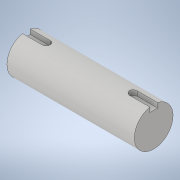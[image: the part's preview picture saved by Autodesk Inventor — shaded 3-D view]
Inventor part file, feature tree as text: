
AUTODESK INVENTOR PART (.ipt)
format: ipt  version: 2021 (Build 250183000, 183)  size: 124,928 bytes
history: native  units: in
note: dims shown in document units (in); Inventor stores cm internally (conversion verified against a paired STEP export)
features: extrude x3, sketch x3, plane x1, mirror x1
ambient origin geometry x8: Origin, YZ Plane, XZ Plane, XY Plane, X Axis, Y Axis, Z Axis, Center Point
bodies: Solid1 (feature_tree)
feature tree (8):
  extrude  "Extrusion1"  Depth=4.107in TaperAngle=0.0deg
  plane  "Work Plane1"
  extrude  "Extrusion6"  Depth=0.15in
  extrude  "Extrusion7"  Depth=0.25in TaperAngle=0.0deg
  mirror  "Mirror2"
  sketch  "Sketch1"  dims[d0=1.25in d1=4.107in d2=0.0in]
  sketch  "Sketch6"  dims[d11=-2.0535in d16=0.15in]
  sketch  "Sketch7"  dims[d17=0.25in d18=0.65in d19=0.0in d20=0.75in d21=0.0in]
